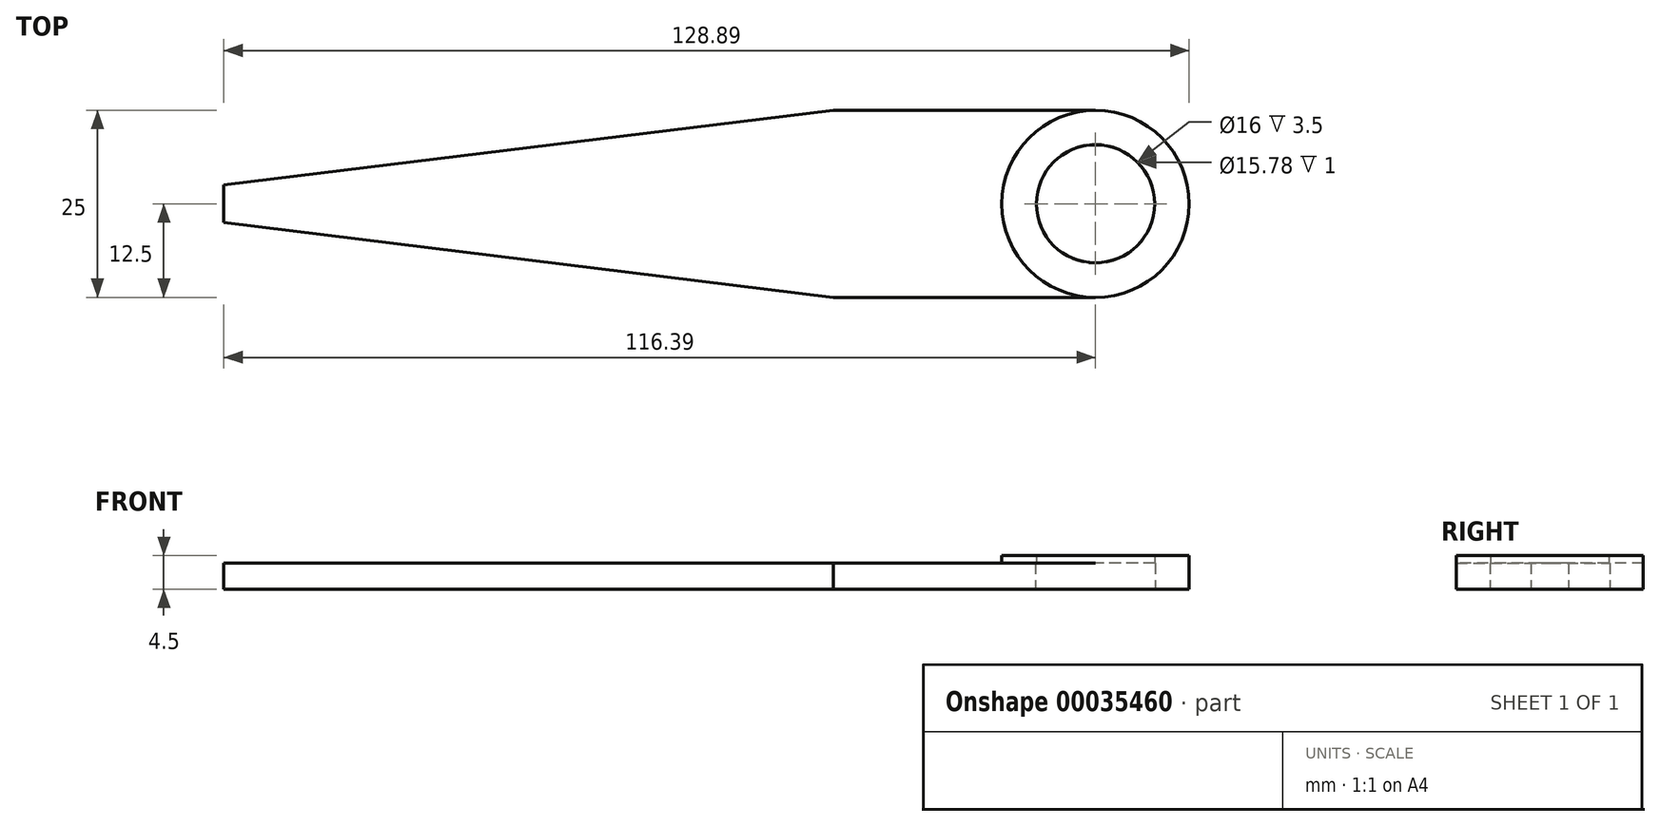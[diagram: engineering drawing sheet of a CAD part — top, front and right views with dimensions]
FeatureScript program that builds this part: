
annotation { "Feature Type Name" : "Feature", "Feature Type Description" : "" }
export const myFeature = defineFeature(function(context is Context, id is Id, definition is map)
    precondition{}
    {
        {
            var Q0;
            Q0=qCreatedBy(makeId("Top.planeOp"),FACE);
            var sketch = newSketch(context, id + "F0", { "sketchPlane" : qUnion([Q0])});
            skCircle(sketch, "E0", {"center": v(0, 0) * mm, "radius": 8 * mm});
            skCircle(sketch, "E1", {"center": v(0, 0) * mm, "radius": 12.5 * mm});
            skLineSegment(sketch, "E2", {"start": v(-35, 12.5) * mm, "end": v(0, 12.5) * mm});
            skLineSegment(sketch, "E3", {"start": v(-35, -12.5) * mm, "end": v(0, -12.5) * mm});
            skLineSegment(sketch, "E4", {"start": v(-35, 12.5) * mm, "end": v(-138.86, 12.5) * mm, "construction": true});
            skLineSegment(sketch, "E5", {"start": v(-35, 12.5) * mm, "end": v(-116.39, 2.5) * mm});
            skLineSegment(sketch, "E6", {"start": v(-35, -12.5) * mm, "end": v(-138.86, -12.5) * mm, "construction": true});
            skLineSegment(sketch, "E7", {"start": v(-35, -12.5) * mm, "end": v(-116.39, -2.5) * mm});
            skLineSegment(sketch, "E8", {"start": v(-116.39, 2.5) * mm, "end": v(-116.39, -2.5) * mm});
            skSolve(sketch);
        }
        {
            var Q0;
            {var subQ1=sQuery(id+"F0.wireOp",EDGE,"E2");Q0=makeQuery(id+"F0.imprint","IMPRINT",FACE,{"disambiguationData":[TD([[makeQuery(id+"F0.imprint","IMPRINT",EDGE,{"derivedFrom":subQ1}),-1.0]])]});}
            var Q1;
            Q1=makeQuery(id+"F0.imprint","IMPRINT",FACE,{"disambiguationData":[TD([[makeQuery(id+"F0.imprint","IMPRINT",EDGE,{"derivedFrom":sQuery(id+"F0.wireOp",EDGE,"E0")}),-1.0]])]});
            extrude(context, id + "F1", {"entities" : qUnion([Q0, Q1]), "depth" : 3.5 * mm});
        }
        {
            var Q0;
            Q0=makeQuery(id+"F1.opExtrude","CAP_FACE",FACE,{"disambiguationData":[OSD([sQuery(id+"F0.wireOp",EDGE,"E0"),sQuery(id+"F0.wireOp",EDGE,"E1"),sQuery(id+"F0.wireOp",EDGE,"E2"),sQuery(id+"F0.wireOp",EDGE,"E3"),sQuery(id+"F0.wireOp",EDGE,"E5"),sQuery(id+"F0.wireOp",EDGE,"E7"),sQuery(id+"F0.wireOp",EDGE,"E8")])],"isStart":false});
            var sketch = newSketch(context, id + "F2", { "sketchPlane" : qUnion([Q0])});
            skCircle(sketch, "E9", {"center": v(0, 0) * mm, "radius": 12.5 * mm});
            skCircle(sketch, "E10", {"center": v(0, 0) * mm, "radius": 7.89 * mm});
            skSolve(sketch);
        }
        {
            var Q0;
            Q0 = qSketchRegion(id + "F2", true);
            extrude(context, id + "F3", {"entities" : qUnion([Q0]), "operationType" : NewBodyOperationType.ADD, "depth" : 1 * mm});
        }
    });
